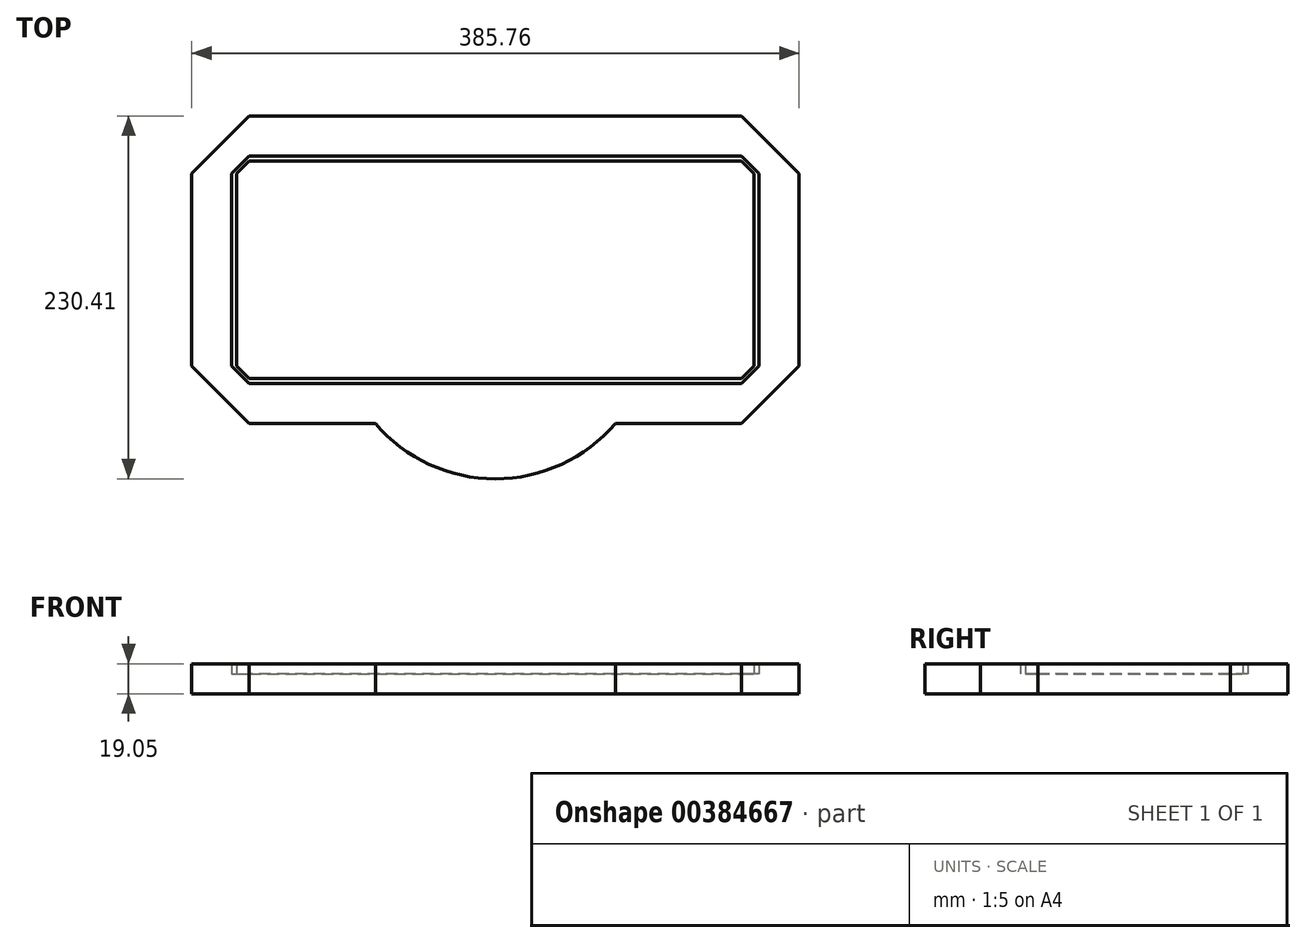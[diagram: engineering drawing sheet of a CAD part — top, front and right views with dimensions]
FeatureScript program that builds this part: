
annotation { "Feature Type Name" : "Feature", "Feature Type Description" : "" }
export const myFeature = defineFeature(function(context is Context, id is Id, definition is map)
    precondition{}
    {
        {
            var Q0;
            Q0=qCreatedBy(makeId("Top.planeOp"),FACE);
            var sketch = newSketch(context, id + "F0", { "sketchPlane" : qUnion([Q0])});
            skLineSegment(sketch, "E0", {"start": v(142.31, 64.99) * mm, "end": v(153.42, 53.88) * mm});
            skLineSegment(sketch, "E1", {"start": v(153.42, -68.35) * mm, "end": v(142.3, -79.47) * mm});
            skLineSegment(sketch, "E2", {"start": v(-181.54, -68.35) * mm, "end": v(-170.41, -79.47) * mm});
            skLineSegment(sketch, "E3", {"start": v(-181.54, 53.86) * mm, "end": v(-170.41, 64.99) * mm});
            skLineSegment(sketch, "E4", {"start": v(-170.41, -79.47) * mm, "end": v(142.3, -79.47) * mm});
            skLineSegment(sketch, "E5", {"start": v(153.42, -68.35) * mm, "end": v(153.42, 53.88) * mm});
            skLineSegment(sketch, "E6", {"start": v(142.31, 64.99) * mm, "end": v(-170.41, 64.99) * mm});
            skLineSegment(sketch, "E7", {"start": v(-181.54, 53.86) * mm, "end": v(-181.54, -68.35) * mm});
            skLineSegment(sketch, "E8.0", {"start": v(142.31, 90.39) * mm, "end": v(-170.41, 90.39) * mm});
            skLineSegment(sketch, "E9.0", {"start": v(-206.94, 53.86) * mm, "end": v(-206.94, -68.35) * mm});
            skLineSegment(sketch, "E10.0", {"start": v(178.82, -68.35) * mm, "end": v(178.82, 53.88) * mm});
            skLineSegment(sketch, "E11", {"start": v(-170.41, 90.39) * mm, "end": v(-206.94, 53.86) * mm});
            skLineSegment(sketch, "E12", {"start": v(-206.94, -68.35) * mm, "end": v(-170.41, -104.87) * mm});
            skLineSegment(sketch, "E13", {"start": v(178.82, -68.35) * mm, "end": v(142.3, -104.87) * mm});
            skLineSegment(sketch, "E14", {"start": v(178.82, 53.88) * mm, "end": v(142.31, 90.39) * mm});
            skArc(sketch, "E15", {"start": v(-90.26, -104.87) * mm, "mid": v(-14.06, -140.02) * mm, "end": v(62.14, -104.87) * mm});
            skLineSegment(sketch, "E16", {"start": v(-170.41, -104.87) * mm, "end": v(-90.26, -104.87) * mm});
            skLineSegment(sketch, "E17", {"start": v(62.14, -104.87) * mm, "end": v(142.3, -104.87) * mm});
            skLineSegment(sketch, "E18.0", {"start": v(-178.36, 53.86) * mm, "end": v(-178.36, -68.35) * mm});
            skLineSegment(sketch, "E19.0", {"start": v(-170.41, -76.3) * mm, "end": v(142.3, -76.3) * mm});
            skLineSegment(sketch, "E20.0", {"start": v(150.25, -68.35) * mm, "end": v(150.25, 53.88) * mm});
            skLineSegment(sketch, "E21.0", {"start": v(142.31, 61.81) * mm, "end": v(-170.41, 61.81) * mm});
            skLineSegment(sketch, "E22", {"start": v(-178.36, -68.35) * mm, "end": v(-170.41, -76.3) * mm});
            skLineSegment(sketch, "E23", {"start": v(142.3, -76.3) * mm, "end": v(150.25, -68.35) * mm});
            skLineSegment(sketch, "E24", {"start": v(150.25, 53.88) * mm, "end": v(142.31, 61.81) * mm});
            skLineSegment(sketch, "E25", {"start": v(-178.36, 53.86) * mm, "end": v(-170.41, 61.81) * mm});
            skSolve(sketch);
        }
        {
            var Q0;
            Q0=makeQuery(id+"F0.imprint","IMPRINT",FACE,{"disambiguationData":[TD([[makeQuery(id+"F0.imprint","IMPRINT",EDGE,{"derivedFrom":sQuery(id+"F0.wireOp",EDGE,"E18.0")}),1.0]])]});
            extrude(context, id + "F1", {"entities" : qUnion([Q0]), "depth" : 19.05 * mm});
        }
        {
            var Q0;
            Q0=makeQuery(id+"F0.imprint","IMPRINT",FACE,{"disambiguationData":[TD([[makeQuery(id+"F0.imprint","IMPRINT",EDGE,{"derivedFrom":sQuery(id+"F0.wireOp",EDGE,"E0")}),-1.0]])]});
            extrude(context, id + "F2", {"entities" : qUnion([Q0]), "operationType" : NewBodyOperationType.ADD, "depth" : 12.7 * mm});
        }
        {
            var Q0;
            Q0=makeQuery(id+"F0.imprint","IMPRINT",FACE,{"disambiguationData":[TD([[makeQuery(id+"F0.imprint","IMPRINT",EDGE,{"derivedFrom":sQuery(id+"F0.wireOp",EDGE,"E0")}),1.0]])]});
            extrude(context, id + "F3", {"entities" : qUnion([Q0]), "operationType" : NewBodyOperationType.ADD, "depth" : 19.05 * mm});
        }
    });
